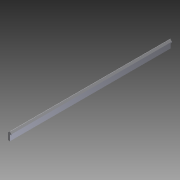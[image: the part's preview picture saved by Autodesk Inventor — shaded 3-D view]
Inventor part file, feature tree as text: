
AUTODESK INVENTOR PART (.ipt)
format: ipt  version: 2014 (Build 180170000, 170)  size: 94,720 bytes
history: native  units: in
note: dims shown in document units (in); Inventor stores cm internally (conversion verified against a paired STEP export)
features: fillet x1, other x1, imported_body x1
ambient origin geometry x8: Origin, YZ Plane, XZ Plane, XY Plane, X Axis, Y Axis, Z Axis, Center Point
bodies: Body1 (feature_tree)
feature tree (3):
  fillet  "Fillet1"  [1 undecoded]
  other  "BWC-T2-SS-11"
  imported_body  "Base1"
note: 1 required parameter value undecoded (feature->parameter linkage not recoverable at this tier; creation-order binding heuristic only, values carry confidence <= 0.55)
